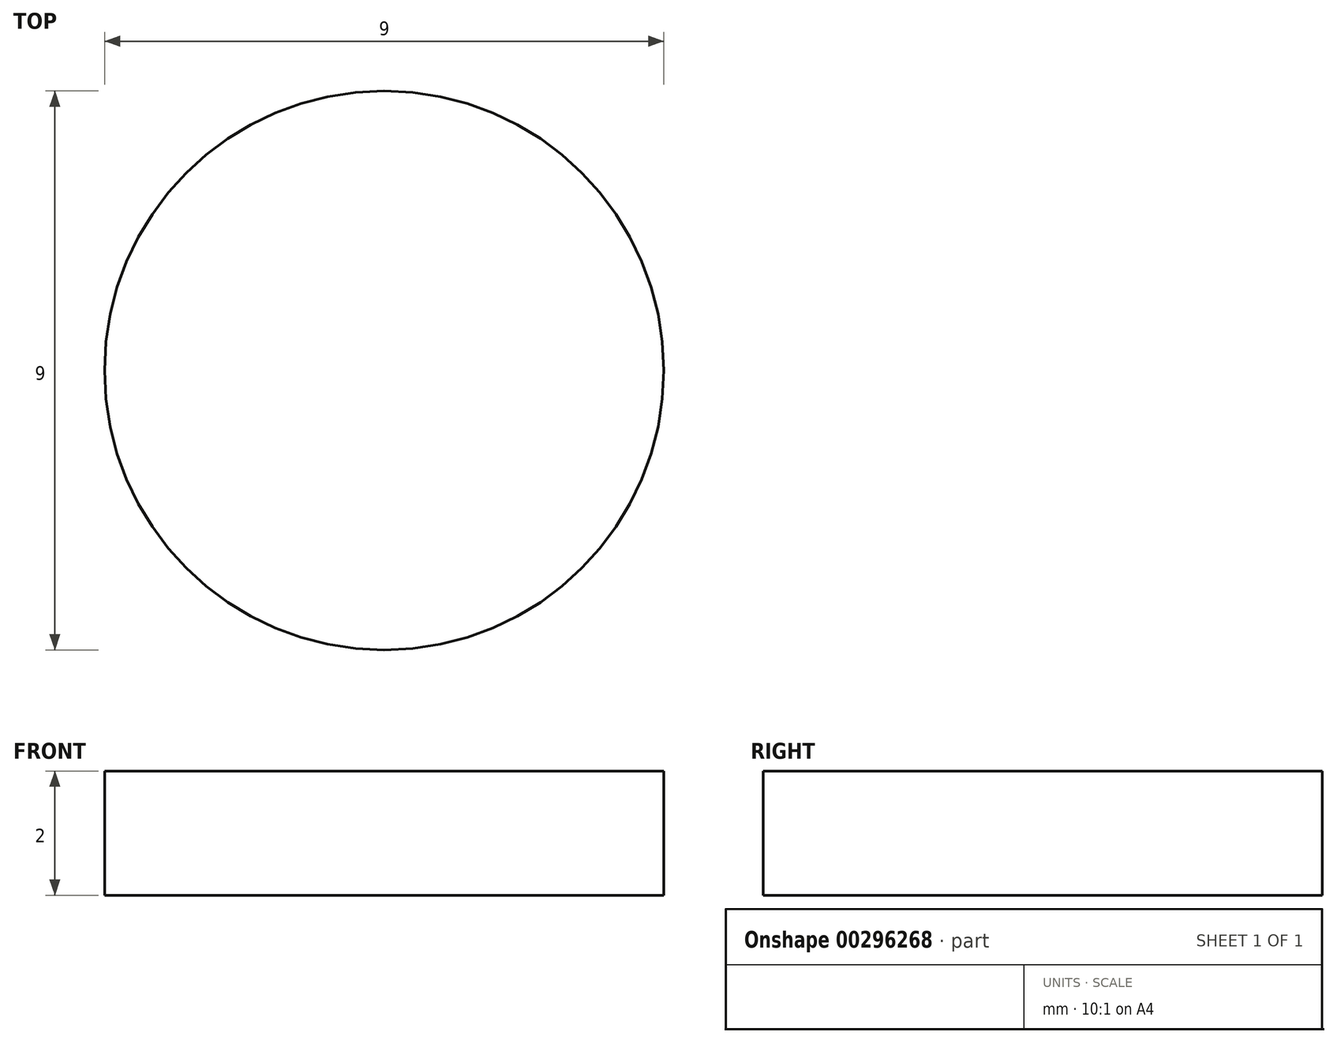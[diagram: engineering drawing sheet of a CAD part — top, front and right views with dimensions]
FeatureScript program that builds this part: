
annotation { "Feature Type Name" : "Feature", "Feature Type Description" : "" }
export const myFeature = defineFeature(function(context is Context, id is Id, definition is map)
    precondition{}
    {
        {
            var Q0;
            Q0=qCreatedBy(makeId("Top.planeOp"),FACE);
            var sketch = newSketch(context, id + "F0", { "sketchPlane" : qUnion([Q0])});
            skCircle(sketch, "E0", {"center": v(0, 0) * mm, "radius": 4.5 * mm});
            skSolve(sketch);
        }
        {
            var Q0;
            Q0=makeQuery(id+"F0.imprint","IMPRINT",FACE,{"disambiguationData":[TD([[makeQuery(id+"F0.imprint","IMPRINT",EDGE,{"derivedFrom":sQuery(id+"F0.wireOp",EDGE,"E0")}),1.0]])]});
            extrude(context, id + "F1", {"entities" : qUnion([Q0]), "depth" : 2 * mm});
        }
    });
